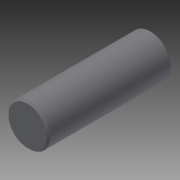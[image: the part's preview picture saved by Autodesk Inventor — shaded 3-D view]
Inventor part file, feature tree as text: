
AUTODESK INVENTOR PART (.ipt)
format: ipt  version: 2014 (Build 180170000, 170)  size: 102,912 bytes
history: native  units: in
note: dims shown in document units (in); Inventor stores cm internally (conversion verified against a paired STEP export)
features: other x35, revolve x1, sketch x1
ambient origin geometry x8: Origin, YZ Plane, XZ Plane, XY Plane, X Axis, Y Axis, Z Axis, Center Point
bodies: Solid1 (feature_tree)
feature tree (37):
  revolve  "Revolution1"  [1 undecoded]
  other  "dia1_XY"
  other  "dia1_YZ"
  other  "dia1_ZX"
  other  "dia1_X"
  other  "dia1_Y"
  other  "dia1_Z"
  other  "dia1_Center"
  other  "dia2_XY"
  other  "dia2_YZ"
  other  "dia2_ZX"
  other  "dia2_X"
  other  "dia2_Y"
  other  "dia2_Z"
  other  "dia2_Center"
  other  "pin_XY"
  other  "pin_YZ"
  other  "pin_ZX"
  other  "pin_X"
  other  "pin_Y"
  other  "pin_Z"
  other  "pin_Center"
  other  "pin1_XY"
  other  "pin1_YZ"
  other  "pin1_ZX"
  other  "pin1_X"
  other  "pin1_Y"
  other  "pin1_Z"
  other  "pin1_Center"
  other  "pin2_XY"
  other  "pin2_YZ"
  other  "pin2_ZX"
  other  "pin2_X"
  other  "pin2_Y"
  other  "pin2_Z"
  other  "pin2_Center"
  sketch  "Sketch_1"  dims[d0=360.0deg]
note: 1 required parameter value undecoded (feature->parameter linkage not recoverable at this tier; creation-order binding heuristic only, values carry confidence <= 0.55)
